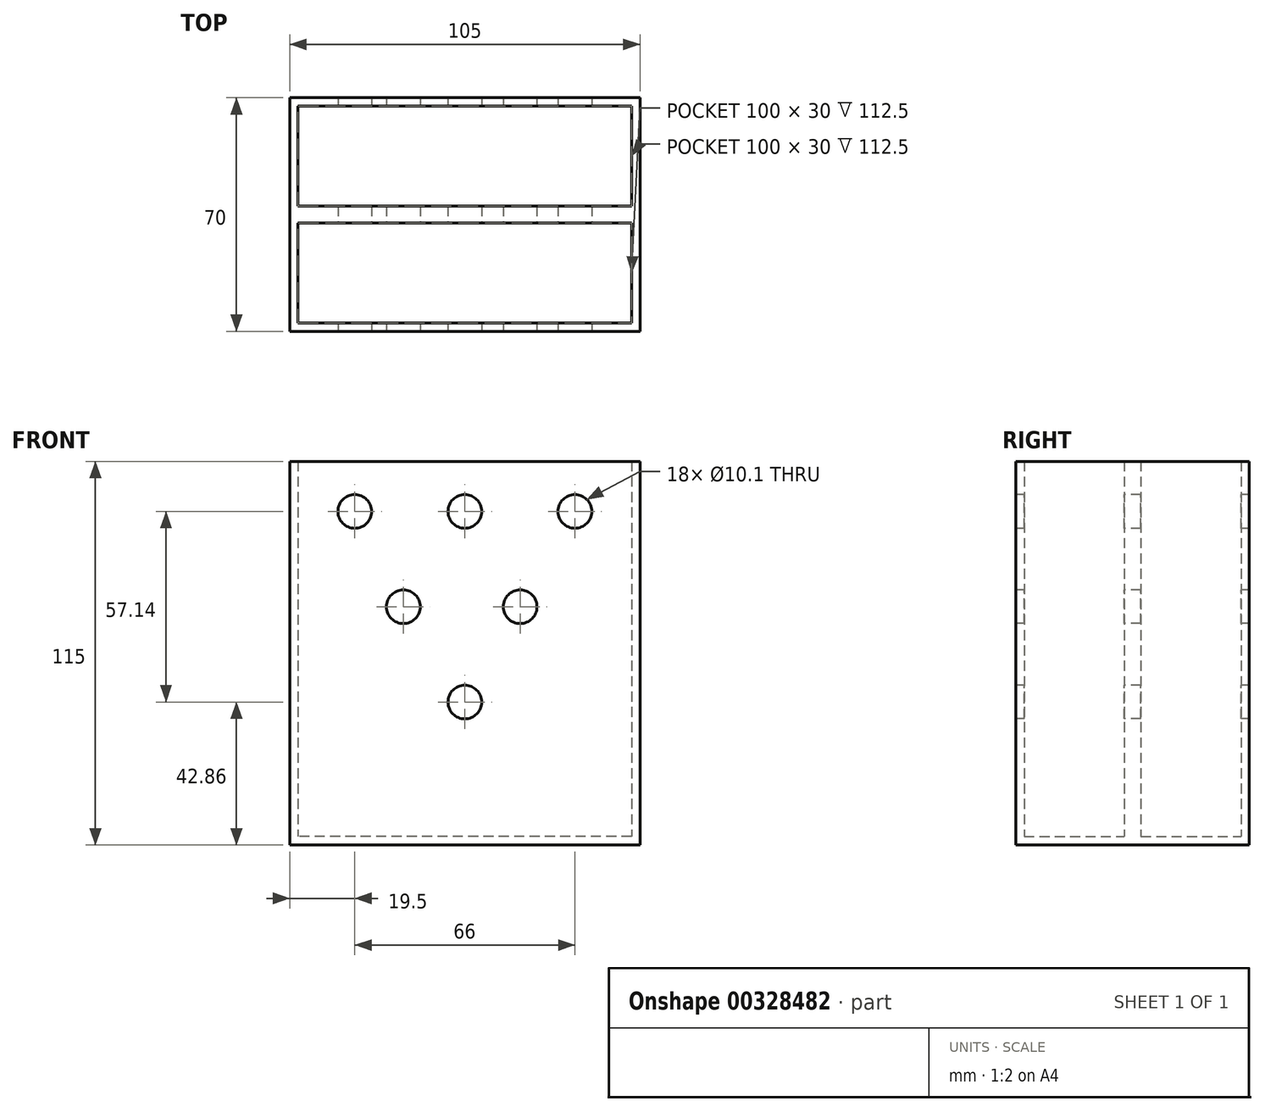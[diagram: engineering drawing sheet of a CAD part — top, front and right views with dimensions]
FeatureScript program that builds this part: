
annotation { "Feature Type Name" : "Feature", "Feature Type Description" : "" }
export const myFeature = defineFeature(function(context is Context, id is Id, definition is map)
    precondition{}
    {
        {
            var Q0;
            Q0=qCreatedBy(makeId("Top.planeOp"),FACE);
            var sketch = newSketch(context, id + "F0", { "sketchPlane" : qUnion([Q0])});
            skLineSegment(sketch, "E0.bottom", {"start": v(52.5, -35) * mm, "end": v(-52.5, -35) * mm});
            skLineSegment(sketch, "E0.top", {"start": v(52.5, 35) * mm, "end": v(-52.5, 35) * mm});
            skLineSegment(sketch, "E0.left", {"start": v(52.5, -35) * mm, "end": v(52.5, 35) * mm});
            skLineSegment(sketch, "E0.right", {"start": v(-52.5, -35) * mm, "end": v(-52.5, 35) * mm});
            skPoint(sketch, "E0.middle", {"position": v(0, 0) * mm});
            skSolve(sketch);
        }
        {
            var Q0;
            Q0=makeQuery(id+"F0.imprint","IMPRINT",FACE,{"disambiguationData":[TD([[makeQuery(id+"F0.imprint","IMPRINT",EDGE,{"derivedFrom":sQuery(id+"F0.wireOp",EDGE,"E0.bottom")}),-1.0]])]});
            extrude(context, id + "F1", {"entities" : qUnion([Q0]), "depth" : 90 * mm, "hasSecondDirection" : true, "secondDirectionOppositeDirection" : true, "secondDirectionDepth" : 25 * mm});
        }
        {
            var Q0;
            Q0=makeQuery(id+"F1.opExtrude","CAP_FACE",FACE,{"disambiguationData":[OSD([sQuery(id+"F0.wireOp",EDGE,"E0.bottom"),sQuery(id+"F0.wireOp",EDGE,"E0.top"),sQuery(id+"F0.wireOp",EDGE,"E0.left"),sQuery(id+"F0.wireOp",EDGE,"E0.right")])],"isStart":false});
            shell(context, id + "F2", {"entities" : qUnion([Q0]), "thickness" : 2.5 * mm});
        }
        {
            var Q0;
            Q0=makeQuery(id+"F2.opShell","OFFSET_FACE",FACE,{"disambiguationData":[OSD([sQuery(id+"F0.wireOp",EDGE,"E0.bottom"),sQuery(id+"F0.wireOp",EDGE,"E0.top"),sQuery(id+"F0.wireOp",EDGE,"E0.left"),sQuery(id+"F0.wireOp",EDGE,"E0.right")])]});
            var sketch = newSketch(context, id + "F3", { "sketchPlane" : qUnion([Q0])});
            skLineSegment(sketch, "E1.bottom", {"start": v(50, -2.5) * mm, "end": v(-50, -2.5) * mm});
            skLineSegment(sketch, "E1.top", {"start": v(50, 2.5) * mm, "end": v(-50, 2.5) * mm});
            skLineSegment(sketch, "E1.left", {"start": v(50, -2.5) * mm, "end": v(50, 2.5) * mm});
            skLineSegment(sketch, "E1.right", {"start": v(-50, -2.5) * mm, "end": v(-50, 2.5) * mm});
            skPoint(sketch, "E1.middle", {"position": v(0, 0) * mm});
            skSolve(sketch);
        }
        {
            var Q0;
            Q0=makeQuery(id+"F2.opShell","OFFSET_FACE",FACE,{"disambiguationData":[OSD([sQuery(id+"F0.wireOp",EDGE,"E0.top")])]});
            var sketch = newSketch(context, id + "F4", { "sketchPlane" : qUnion([Q0])});
            skLineSegment(sketch, "E2", {"start": v(-35, 75) * mm, "end": v(35, 75) * mm, "construction": true});
            skLineSegment(sketch, "E3", {"start": v(0, 65) * mm, "end": v(0, -22.5) * mm, "construction": true});
            skCircle(sketch, "E4", {"center": v(0, 75) * mm, "radius": 5.05 * mm});
            skCircle(sketch, "E5", {"center": v(33, 75) * mm, "radius": 5.05 * mm});
            skCircle(sketch, "E6", {"center": v(-33, 75) * mm, "radius": 5.05 * mm});
            skLineSegment(sketch, "E7", {"start": v(-18.43, 75) * mm, "end": v(-18.43, -22.5) * mm, "construction": true});
            skLineSegment(sketch, "E8", {"start": v(16.57, 75) * mm, "end": v(16.57, -22.5) * mm, "construction": true});
            skCircle(sketch, "E9", {"center": v(-18.43, 46.43) * mm, "radius": 5.05 * mm});
            skCircle(sketch, "E10", {"center": v(16.57, 46.43) * mm, "radius": 5.05 * mm});
            skCircle(sketch, "E11", {"center": v(0, 17.86) * mm, "radius": 5.05 * mm});
            skSolve(sketch);
        }
        {
            var Q0;
            Q0=makeQuery(id+"F3.imprint","IMPRINT",FACE,{"disambiguationData":[TD([[makeQuery(id+"F3.imprint","IMPRINT",EDGE,{"derivedFrom":sQuery(id+"F3.wireOp",EDGE,"E1.bottom")}),-1.0]])]});
            var Q1;
            {var subQ0=sQuery(id+"F0.wireOp",EDGE,"E0.top");Q1=makeQuery(id+"Fh13vaunErIq6qI_1.boolean.opBoolean","MERGE",FACE,{"derivedFrom":[makeQuery(id+"F1.opExtrude","CAP_FACE",FACE,{"disambiguationData":[OSD([sQuery(id+"F0.wireOp",EDGE,"E0.bottom"),subQ0,sQuery(id+"F0.wireOp",EDGE,"E0.left"),sQuery(id+"F0.wireOp",EDGE,"E0.right")])],"isStart":false}),makeQuery(id+"Fh13vaunErIq6qI_1.opExtrude","SWEPT_FACE",FACE,{"disambiguationData":[OSD([subQ0]),TDD([makeQuery(id+"F1.opExtrude","CAP_EDGE",EDGE,{"disambiguationData":[OSD([subQ0])],"isStart":false})])]})]});}
            extrude(context, id + "F5", {"entities" : qUnion([Q0]), "operationType" : NewBodyOperationType.ADD, "endBound" : BoundingType.UP_TO_SURFACE, "endBoundEntityFace" : qUnion([Q1]), "depth" : 62.5 * mm});
        }
        {
            var Q0;
            Q0 = qSketchRegion(id + "F4", true);
            var Q1;
            Q1=makeQuery(id+"F1.opExtrude","SWEPT_FACE",FACE,{"disambiguationData":[OSD([sQuery(id+"F0.wireOp",EDGE,"E0.bottom")])]});
            extrude(context, id + "F6", {"entities" : qUnion([Q0]), "operationType" : NewBodyOperationType.REMOVE, "oppositeDirection" : true, "depth" : 2.5 * mm, "hasSecondDirection" : true, "secondDirectionBound" : SecondDirectionBoundingType.UP_TO_SURFACE, "secondDirectionOppositeDirection" : false, "secondDirectionBoundEntityFace" : qUnion([Q1]), "secondDirectionDepth" : 25 * mm});
        }
    });
